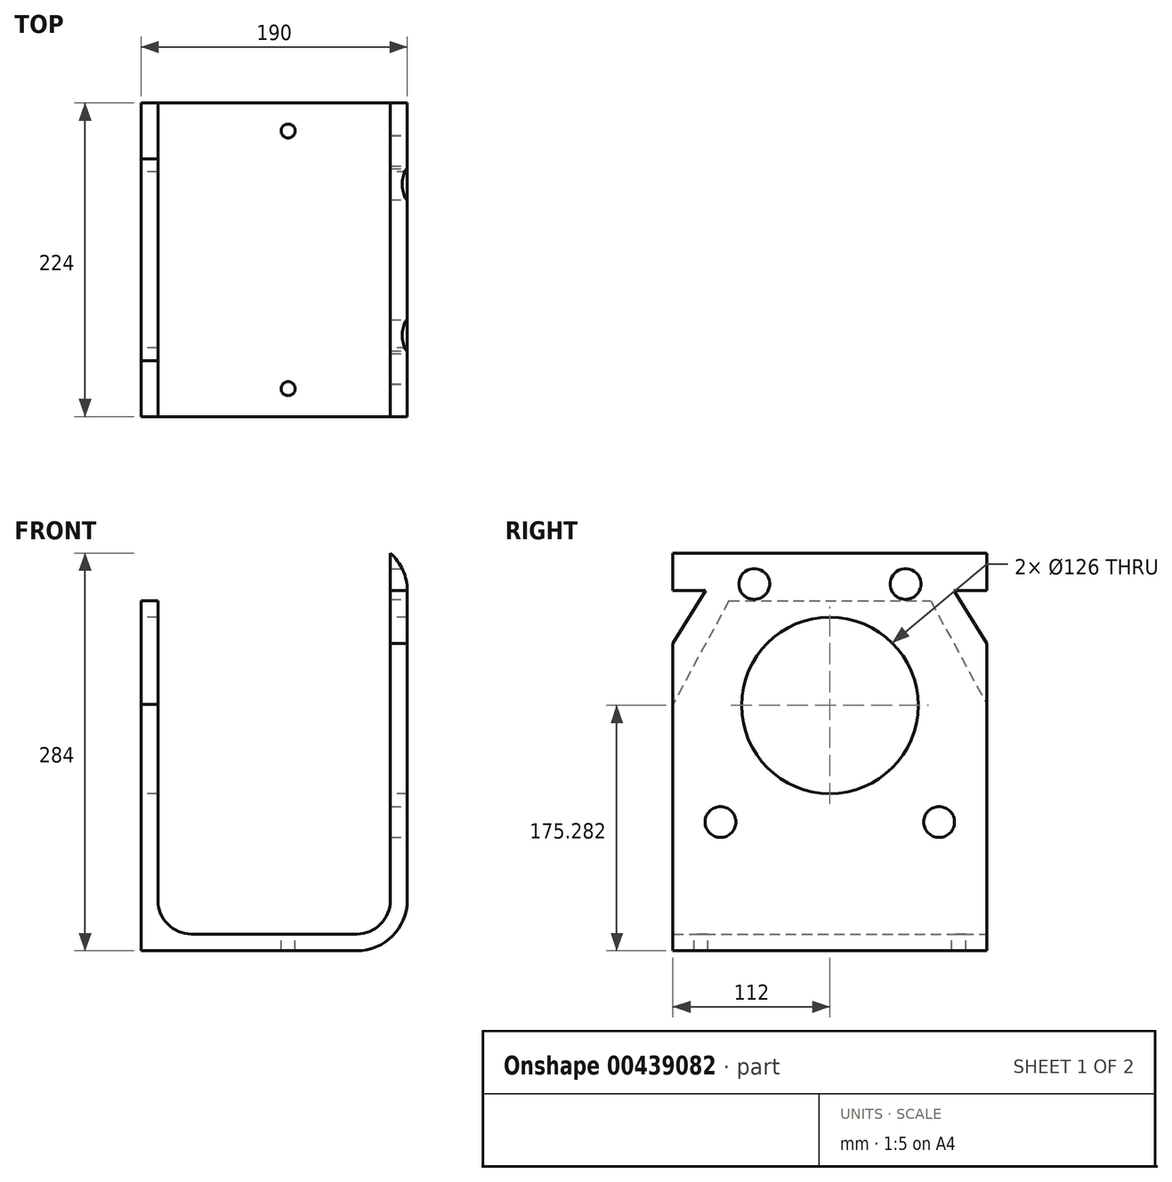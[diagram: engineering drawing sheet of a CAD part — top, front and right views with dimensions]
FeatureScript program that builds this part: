
annotation { "Feature Type Name" : "Feature", "Feature Type Description" : "" }
export const myFeature = defineFeature(function(context is Context, id is Id, definition is map)
    precondition{}
    {
        {
            var Q0;
            Q0=qCreatedBy(makeId("Front.planeOp"),FACE);
            var sketch = newSketch(context, id + "F0", { "sketchPlane" : qUnion([Q0])});
            skLineSegment(sketch, "E0.bottom", {"start": v(-35.67, 188.2) * mm, "end": v(-23.67, 188.2) * mm});
            skLineSegment(sketch, "E0.top", {"start": v(-35.67, -61.8) * mm, "end": v(-23.67, -61.8) * mm});
            skLineSegment(sketch, "E0.left", {"start": v(-35.67, 188.2) * mm, "end": v(-35.67, -61.8) * mm});
            skLineSegment(sketch, "E0.right", {"start": v(-23.67, 188.2) * mm, "end": v(-23.67, -61.8) * mm});
            skLineSegment(sketch, "E1.bottom", {"start": v(-35.67, -61.8) * mm, "end": v(154.33, -61.8) * mm});
            skLineSegment(sketch, "E1.top", {"start": v(-35.67, -49.8) * mm, "end": v(154.33, -49.8) * mm});
            skLineSegment(sketch, "E1.left", {"start": v(-35.67, -61.8) * mm, "end": v(-35.67, -49.8) * mm});
            skLineSegment(sketch, "E1.right", {"start": v(154.33, -61.8) * mm, "end": v(154.33, -49.8) * mm});
            skLineSegment(sketch, "E2.bottom", {"start": v(154.33, -61.8) * mm, "end": v(142.33, -61.8) * mm});
            skLineSegment(sketch, "E2.top", {"start": v(154.33, 222.2) * mm, "end": v(142.33, 222.2) * mm});
            skLineSegment(sketch, "E2.left", {"start": v(154.33, -61.8) * mm, "end": v(154.33, 222.2) * mm});
            skLineSegment(sketch, "E2.right", {"start": v(142.33, -61.8) * mm, "end": v(142.33, 222.2) * mm});
            skSolve(sketch);
        }
        {
            var Q0;
            Q0=qSketchRegion(id+"F0",true);
            extrude(context, id + "F1", {"entities" : qUnion([Q0]), "depth" : 224 * mm});
        }
        {
            var Q0;
            Q0=makeQuery(id+"F1.opExtrude","SWEPT_EDGE",EDGE,{"disambiguationData":[OSD([sQuery(id+"F0.wireOp",EDGE,"E0.right"),sQuery(id+"F0.wireOp",EDGE,"E1.top")])]});
            var Q1;
            Q1=makeQuery(id+"F1.opExtrude","SWEPT_EDGE",EDGE,{"disambiguationData":[OSD([sQuery(id+"F0.wireOp",EDGE,"E1.top"),sQuery(id+"F0.wireOp",EDGE,"E2.right")])]});
            fillet(context, id + "F2", {"entities" : qUnion([Q0, Q1]), "radius" : 24 * mm, "tangentPropagation" : true, "allowEdgeOverflow" : false});
        }
        {
            var Q0;
            Q0=makeQuery(id+"F1.opExtrude","SWEPT_EDGE",EDGE,{"disambiguationData":[OSD([sQuery(id+"F0.wireOp",EDGE,"E2.bottom"),sQuery(id+"F0.wireOp",EDGE,"E2.left")])]});
            var Q1;
            Q1=makeQuery(id+"F1.opExtrude","SWEPT_EDGE",EDGE,{"disambiguationData":[OSD([sQuery(id+"F0.wireOp",EDGE,"E1.bottom"),sQuery(id+"F0.wireOp",EDGE,"E1.left")])]});
            fillet(context, id + "F3", {"entities" : qUnion([Q0, Q1]), "radius" : 36 * mm, "tangentPropagation" : true, "allowEdgeOverflow" : false});
        }
        {
            var Q0;
            Q0=makeQuery(id+"F1.opExtrude","SWEPT_FACE",FACE,{"disambiguationData":[OSD([sQuery(id+"F0.wireOp",EDGE,"E0.left"),sQuery(id+"F0.wireOp",EDGE,"E1.left")])]});
            var sketch = newSketch(context, id + "F4", { "sketchPlane" : qUnion([Q0])});
            skLineSegment(sketch, "E3", {"start": v(184, 188.2) * mm, "end": v(224, 114.33) * mm});
            skLineSegment(sketch, "E4", {"start": v(40, 188.2) * mm, "end": v(0, 114.33) * mm});
            skSolve(sketch);
        }
        {
            var Q0;
            {var subQ0=sQuery(id+"F4.wireOp",EDGE,"E4");Q0=makeQuery(id+"F4.imprint","IMPRINT",FACE,{"disambiguationData":[TD([[makeQuery(id+"F4.imprint","IMPRINT",EDGE,{"derivedFrom":subQ0}),-1.0]])]});}
            var Q1;
            {var subQ0=sQuery(id+"F4.wireOp",EDGE,"E3");Q1=makeQuery(id+"F4.imprint","IMPRINT",FACE,{"disambiguationData":[TD([[makeQuery(id+"F4.imprint","IMPRINT",EDGE,{"derivedFrom":subQ0}),1.0]])]});}
            extrude(context, id + "F5", {"entities" : qUnion([Q0, Q1]), "operationType" : NewBodyOperationType.REMOVE, "oppositeDirection" : true, "depth" : 12 * mm});
        }
        {
            var Q0;
            Q0=makeQuery(id+"F1.opExtrude","SWEPT_FACE",FACE,{"disambiguationData":[OSD([sQuery(id+"F0.wireOp",EDGE,"E2.left")])]});
            var sketch = newSketch(context, id + "F6", { "sketchPlane" : qUnion([Q0])});
            skLineSegment(sketch, "E5", {"start": v(-224, 157.58) * mm, "end": v(-184, 222.2) * mm});
            skLineSegment(sketch, "E6", {"start": v(-40, 222.2) * mm, "end": v(0, 157.58) * mm});
            skSolve(sketch);
        }
        {
            var Q0;
            {var subQ0=sQuery(id+"F6.wireOp",EDGE,"E5");Q0=makeQuery(id+"F6.imprint","IMPRINT",FACE,{"disambiguationData":[TD([[makeQuery(id+"F6.imprint","IMPRINT",EDGE,{"derivedFrom":subQ0}),1.0]])]});}
            var Q1;
            {var subQ0=sQuery(id+"F6.wireOp",EDGE,"E6");Q1=makeQuery(id+"F6.imprint","IMPRINT",FACE,{"disambiguationData":[TD([[makeQuery(id+"F6.imprint","IMPRINT",EDGE,{"derivedFrom":subQ0}),1.0]])]});}
            extrude(context, id + "F7", {"entities" : qUnion([Q0, Q1]), "operationType" : NewBodyOperationType.REMOVE, "oppositeDirection" : true, "depth" : 12 * mm});
        }
        {
            var Q0;
            Q0=makeQuery(id+"F1.opExtrude","SWEPT_FACE",FACE,{"disambiguationData":[OSD([sQuery(id+"F0.wireOp",EDGE,"E0.left"),sQuery(id+"F0.wireOp",EDGE,"E1.left")])]});
            var sketch = newSketch(context, id + "F8", { "sketchPlane" : qUnion([Q0])});
            skCircle(sketch, "E7", {"center": v(112, 113.48) * mm, "radius": 63 * mm});
            skSolve(sketch);
        }
        {
            var Q0;
            Q0=qSketchRegion(id+"F8",true);
            extrude(context, id + "F9", {"entities" : qUnion([Q0]), "operationType" : NewBodyOperationType.REMOVE, "oppositeDirection" : true, "depth" : 190 * mm});
        }
        {
            var Q0;
            Q0=makeQuery(id+"F1.opExtrude","SWEPT_FACE",FACE,{"disambiguationData":[OSD([sQuery(id+"F0.wireOp",EDGE,"E2.left")])]});
            var sketch = newSketch(context, id + "F10", { "sketchPlane" : qUnion([Q0])});
            skCircle(sketch, "E8", {"center": v(-166, 200.2) * mm, "radius": 11 * mm});
            skCircle(sketch, "E9", {"center": v(-58, 200.2) * mm, "radius": 11 * mm});
            skCircle(sketch, "E10", {"center": v(-34, 30.2) * mm, "radius": 11 * mm});
            skCircle(sketch, "E11", {"center": v(-190, 30.2) * mm, "radius": 11 * mm});
            skSolve(sketch);
        }
        {
            var Q0;
            Q0=qSketchRegion(id+"F10",true);
            extrude(context, id + "F11", {"entities" : qUnion([Q0]), "operationType" : NewBodyOperationType.REMOVE, "oppositeDirection" : true, "depth" : 25 * mm});
        }
        {
            var Q0;
            Q0=makeQuery(id+"F1.opExtrude","SWEPT_FACE",FACE,{"disambiguationData":[OSD([sQuery(id+"F0.wireOp",EDGE,"E1.top")])]});
            var sketch = newSketch(context, id + "F12", { "sketchPlane" : qUnion([Q0])});
            skCircle(sketch, "E12", {"center": v(69.33, -204) * mm, "radius": 5 * mm});
            skCircle(sketch, "E13", {"center": v(69.33, -20) * mm, "radius": 5 * mm});
            skSolve(sketch);
        }
        {
            var Q0;
            Q0 = qSketchRegion(id + "F12", true);
            extrude(context, id + "F13", {"entities" : qUnion([Q0]), "operationType" : NewBodyOperationType.REMOVE, "oppositeDirection" : true, "depth" : 25 * mm});
        }
    });
